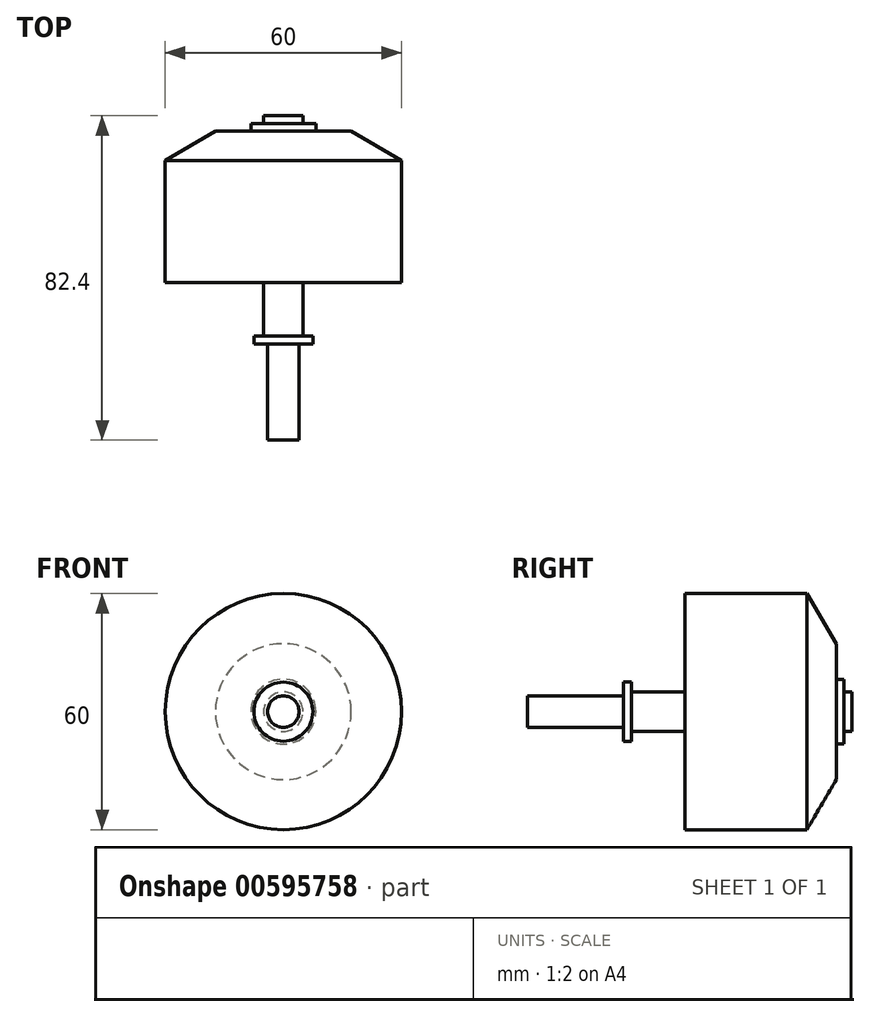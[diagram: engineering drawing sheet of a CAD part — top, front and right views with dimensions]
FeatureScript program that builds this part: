
annotation { "Feature Type Name" : "Feature", "Feature Type Description" : "" }
export const myFeature = defineFeature(function(context is Context, id is Id, definition is map)
    precondition{}
    {
        {
            var Q0;
            Q0=qCreatedBy(makeId("Right.planeOp"),FACE);
            var sketch = newSketch(context, id + "F0", { "sketchPlane" : qUnion([Q0])});
            skLineSegment(sketch, "E0", {"start": v(-40, 0) * mm, "end": v(42.4, 0) * mm});
            skLineSegment(sketch, "E1", {"start": v(-40, 0) * mm, "end": v(-40, 4) * mm});
            skLineSegment(sketch, "E2", {"start": v(-40, 4) * mm, "end": v(0, 4) * mm});
            skLineSegment(sketch, "E3", {"start": v(0, 4) * mm, "end": v(0, 30) * mm});
            skLineSegment(sketch, "E4", {"start": v(0, 30) * mm, "end": v(31, 30) * mm});
            skLineSegment(sketch, "E5", {"start": v(31, 30) * mm, "end": v(38.5, 17.25) * mm});
            skLineSegment(sketch, "E6", {"start": v(38.5, 17.25) * mm, "end": v(38.5, 8.25) * mm});
            skLineSegment(sketch, "E7", {"start": v(38.5, 8.25) * mm, "end": v(40.4, 8.25) * mm});
            skLineSegment(sketch, "E8", {"start": v(40.4, 8.25) * mm, "end": v(40.4, 5) * mm});
            skLineSegment(sketch, "E9", {"start": v(40.4, 5) * mm, "end": v(42.4, 5) * mm});
            skLineSegment(sketch, "E10", {"start": v(42.4, 5) * mm, "end": v(42.4, 0) * mm});
            skSolve(sketch);
        }
        {
            var Q0;
            Q0 = qSketchRegion(id + "F0", true);
            var Q1;
            Q1=sQuery(id+"F0.wireOp",EDGE,"E0");
            revolve(context, id + "F1", {"entities" : qUnion([Q0]), "axis" : qUnion([Q1]), "revolveType" : RevolveType.FULL});
        }
        {
            var Q0;
            Q0=makeQuery(id+"F1.opRevolve","SWEPT_FACE",FACE,{"disambiguationData":[OSD([sQuery(id+"F0.wireOp",EDGE,"E3")])]});
            var sketch = newSketch(context, id + "F2", { "sketchPlane" : qUnion([Q0])});
            skCircle(sketch, "E11", {"center": v(0, 0) * mm, "radius": 5 * mm});
            skSolve(sketch);
        }
        {
            var Q0;
            Q0 = qSketchRegion(id + "F2", true);
            extrude(context, id + "F3", {"entities" : qUnion([Q0]), "operationType" : NewBodyOperationType.ADD, "depth" : 13.6 * mm, "offsetDistance" : 25 * mm});
        }
        {
            var Q0;
            Q0=qCreatedBy(makeId("Right.planeOp"),FACE);
            var sketch = newSketch(context, id + "F4", { "sketchPlane" : qUnion([Q0])});
            skLineSegment(sketch, "E12", {"start": v(0, 0) * mm, "end": v(-24.2, 0) * mm, "construction": true});
            skLineSegment(sketch, "E13.bottom", {"start": v(-15.6, 0) * mm, "end": v(-13.6, 0) * mm});
            skLineSegment(sketch, "E13.top", {"start": v(-15.6, 7.5) * mm, "end": v(-13.6, 7.5) * mm});
            skLineSegment(sketch, "E13.left", {"start": v(-15.6, 0) * mm, "end": v(-15.6, 7.5) * mm});
            skLineSegment(sketch, "E13.right", {"start": v(-13.6, 0) * mm, "end": v(-13.6, 7.5) * mm});
            skLineSegment(sketch, "E14.0", {"start": v(-13.6, -5) * mm, "end": v(-13.6, 5) * mm, "construction": true});
            skSolve(sketch);
        }
        {
            var Q0;
            Q0=makeQuery(id+"F4.imprint","IMPRINT",FACE,{"disambiguationData":[TD([[makeQuery(id+"F4.imprint","IMPRINT",EDGE,{"derivedFrom":sQuery(id+"F4.wireOp",EDGE,"E13.bottom")}),1.0]])]});
            var Q1;
            Q1=sQuery(id+"F4.wireOp",EDGE,"E13.bottom");
            revolve(context, id + "F5", {"operationType" : NewBodyOperationType.ADD, "entities" : qUnion([Q0]), "axis" : qUnion([Q1]), "revolveType" : RevolveType.FULL});
        }
    });
